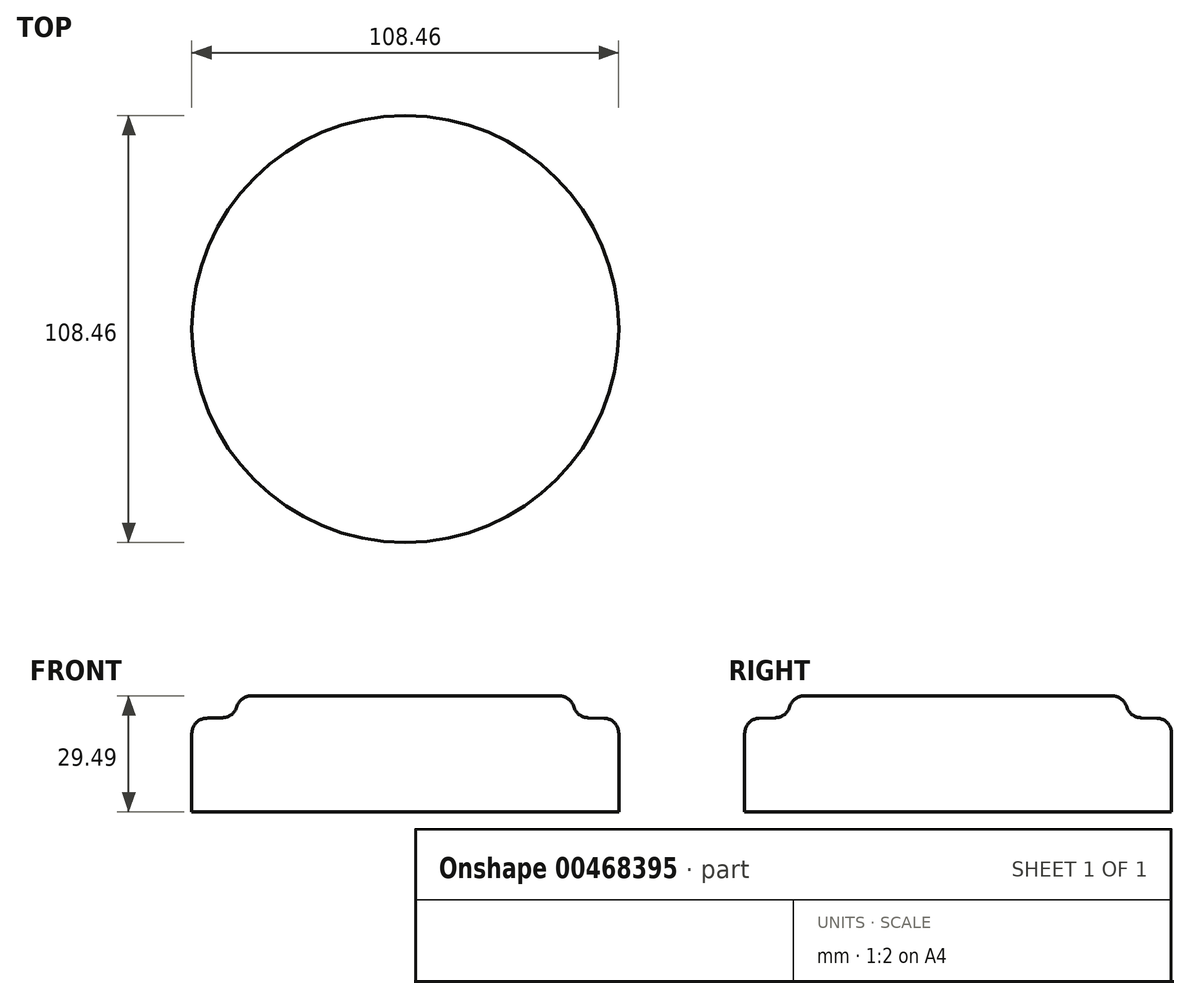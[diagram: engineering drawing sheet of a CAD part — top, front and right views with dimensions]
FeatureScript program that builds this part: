
annotation { "Feature Type Name" : "Feature", "Feature Type Description" : "" }
export const myFeature = defineFeature(function(context is Context, id is Id, definition is map)
    precondition{}
    {
        {
            var Q0;
            Q0=qCreatedBy(makeId("Front.planeOp"),FACE);
            var sketch = newSketch(context, id + "F0", { "sketchPlane" : qUnion([Q0])});
            skLineSegment(sketch, "E0", {"start": v(0, 0) * mm, "end": v(0, 25.35) * mm});
            skLineSegment(sketch, "E1", {"start": v(0, 25.35) * mm, "end": v(39.15, 25.35) * mm});
            skLineSegment(sketch, "E2", {"start": v(42.96, 21.54) * mm, "end": v(42.96, 19.93) * mm});
            skLineSegment(sketch, "E3", {"start": v(46.36, 19.82) * mm, "end": v(50.55, 19.68) * mm});
            skLineSegment(sketch, "E4", {"start": v(54.23, 15.88) * mm, "end": v(54.23, -4.14) * mm});
            skLineSegment(sketch, "E5", {"start": v(54.23, -4.14) * mm, "end": v(0, -4.14) * mm});
            skLineSegment(sketch, "E6", {"start": v(0, -4.14) * mm, "end": v(0, 0) * mm});
            skPoint(sketch, "E7.visualSharp", {"position": v(42.96, 25.35) * mm});
            skArc(sketch, "E7.filletArc", {"start": v(42.82, 22.58) * mm, "mid": v(41.45, 24.58) * mm, "end": v(39.15, 25.35) * mm});
            skArc(sketch, "E8.filletArc", {"start": v(42.82, 22.58) * mm, "mid": v(44.14, 20.63) * mm, "end": v(46.36, 19.82) * mm});
            skPoint(sketch, "E9.visualSharp", {"position": v(54.23, 19.56) * mm});
            skArc(sketch, "E9.filletArc", {"start": v(54.23, 15.88) * mm, "mid": v(53.16, 18.53) * mm, "end": v(50.55, 19.68) * mm});
            skSolve(sketch);
        }
        {
            var Q0;
            Q0=makeQuery(id+"F0.imprint","IMPRINT",FACE,{"disambiguationData":[TD([[makeQuery(id+"F0.imprint","IMPRINT",EDGE,{"derivedFrom":sQuery(id+"F0.wireOp",EDGE,"E0")}),-1.0]])]});
            var Q1;
            Q1=sQuery(id+"F0.wireOp",EDGE,"E0");
            revolve(context, id + "F1", {"entities" : qUnion([Q0]), "axis" : qUnion([Q1]), "revolveType" : RevolveType.FULL});
        }
    });
